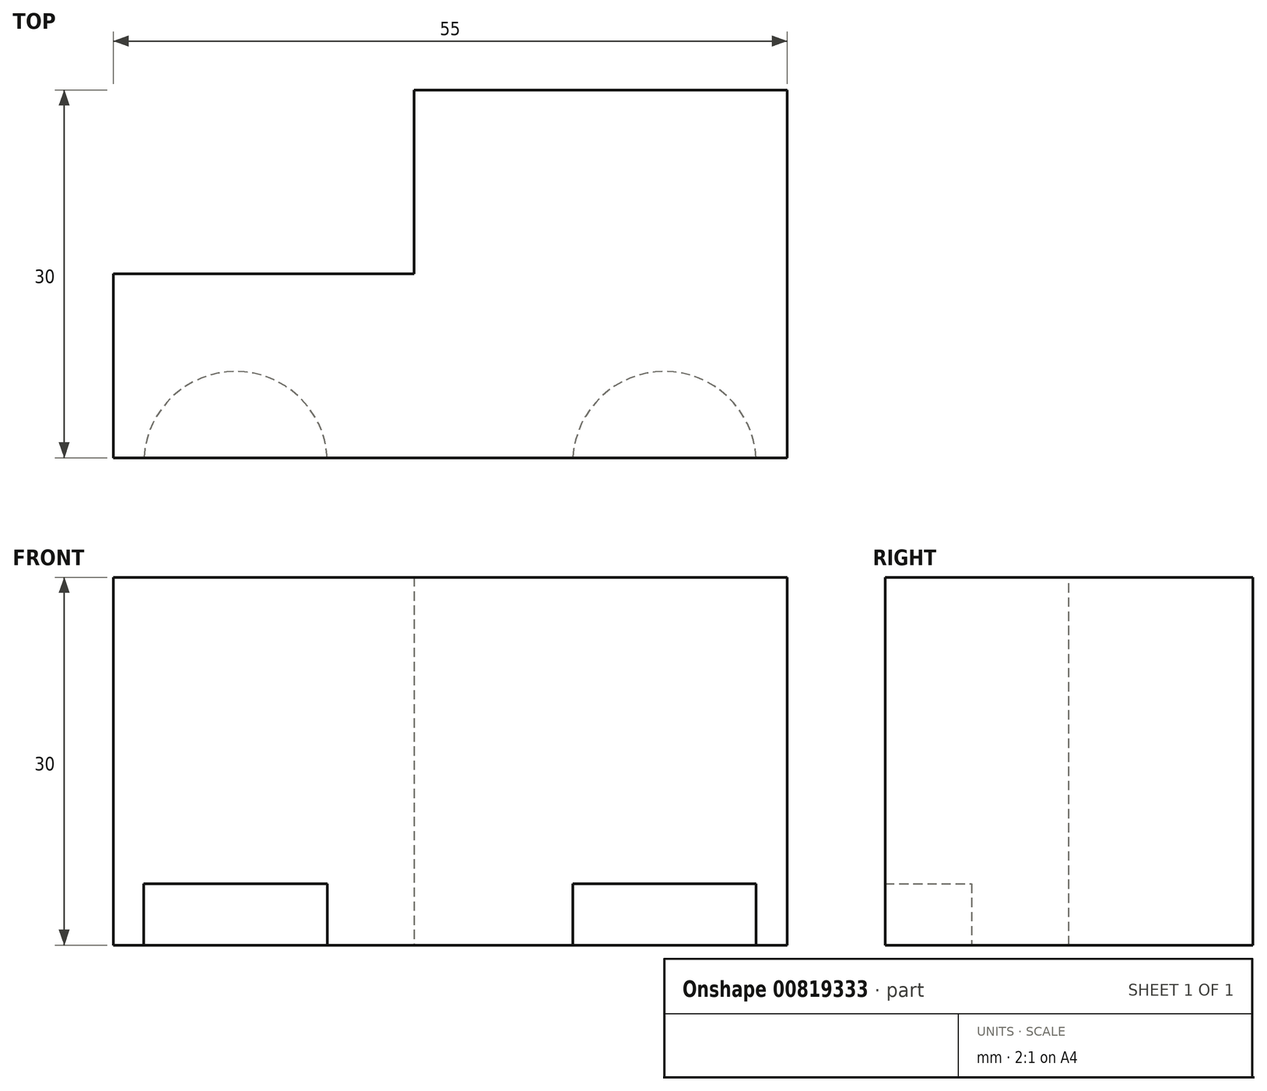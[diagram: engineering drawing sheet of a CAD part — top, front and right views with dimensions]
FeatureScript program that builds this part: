
annotation { "Feature Type Name" : "Feature", "Feature Type Description" : "" }
export const myFeature = defineFeature(function(context is Context, id is Id, definition is map)
    precondition{}
    {
        {
            var Q0;
            Q0=qCreatedBy(makeId("Top.planeOp"),FACE);
            var sketch = newSketch(context, id + "F0", { "sketchPlane" : qUnion([Q0])});
            skLineSegment(sketch, "E0.bottom", {"start": v(-27.5, 15) * mm, "end": v(27.5, 15) * mm});
            skLineSegment(sketch, "E0.top", {"start": v(-27.5, -15) * mm, "end": v(27.5, -15) * mm});
            skLineSegment(sketch, "E0.left", {"start": v(-27.5, 15) * mm, "end": v(-27.5, -15) * mm});
            skLineSegment(sketch, "E0.right", {"start": v(27.5, 15) * mm, "end": v(27.5, -15) * mm});
            skPoint(sketch, "E0.middle", {"position": v(0, 0) * mm});
            skSolve(sketch);
        }
        {
            var Q0;
            Q0=makeQuery(id+"F0.imprint","IMPRINT",FACE,{"disambiguationData":[TD([[makeQuery(id+"F0.imprint","IMPRINT",EDGE,{"derivedFrom":sQuery(id+"F0.wireOp",EDGE,"E0.bottom")}),-1.0]])]});
            extrude(context, id + "F1", {"entities" : qUnion([Q0]), "depth" : 30 * mm, "offsetDistance" : 25 * mm});
        }
        {
            var Q0;
            Q0=qCreatedBy(makeId("Top.planeOp"),FACE);
            var sketch = newSketch(context, id + "F2", { "sketchPlane" : qUnion([Q0])});
            skLineSegment(sketch, "E1.bottom", {"start": v(-28.1, 16) * mm, "end": v(-2.95, 16) * mm});
            skLineSegment(sketch, "E1.top", {"start": v(-28.1, 0) * mm, "end": v(-2.95, 0) * mm});
            skLineSegment(sketch, "E1.left", {"start": v(-28.1, 16) * mm, "end": v(-28.1, 0) * mm});
            skLineSegment(sketch, "E1.right", {"start": v(-2.95, 16) * mm, "end": v(-2.95, 0) * mm});
            skSolve(sketch);
        }
        {
            var Q0;
            Q0 = qSketchRegion(id + "F2", true);
            extrude(context, id + "F3", {"entities" : qUnion([Q0]), "operationType" : NewBodyOperationType.REMOVE, "depth" : 67.1 * mm, "offsetDistance" : 25 * mm});
        }
        {
            var Q0;
            Q0=qCreatedBy(makeId("Top.planeOp"),FACE);
            var sketch = newSketch(context, id + "F4", { "sketchPlane" : qUnion([Q0])});
            skCircle(sketch, "E2", {"center": v(-17.51, -15.46) * mm, "radius": 7.5 * mm});
            skCircle(sketch, "E3.1.0.0", {"center": v(17.49, -15.46) * mm, "radius": 7.5 * mm});
            skLineSegment(sketch, "E3.direction1", {"start": v(-17.51, -15.46) * mm, "end": v(17.49, -15.46) * mm, "construction": true});
            skSolve(sketch);
        }
        {
            var Q0;
            Q0=makeQuery(id+"F4.imprint","IMPRINT",FACE,{"disambiguationData":[TD([[makeQuery(id+"F4.imprint","IMPRINT",EDGE,{"derivedFrom":sQuery(id+"F4.wireOp",EDGE,"E3.1.0.0")}),1.0]])]});
            extrude(context, id + "F5", {"entities" : qUnion([Q0]), "operationType" : NewBodyOperationType.REMOVE, "oppositeDirection" : true, "depth" : -5 * mm, "offsetDistance" : 25 * mm});
        }
        {
            var Q0;
            Q0 = qSketchRegion(id + "F4", true);
            extrude(context, id + "F6", {"entities" : qUnion([Q0]), "operationType" : NewBodyOperationType.REMOVE, "oppositeDirection" : true, "depth" : -5 * mm, "offsetDistance" : 25 * mm});
        }
    });
